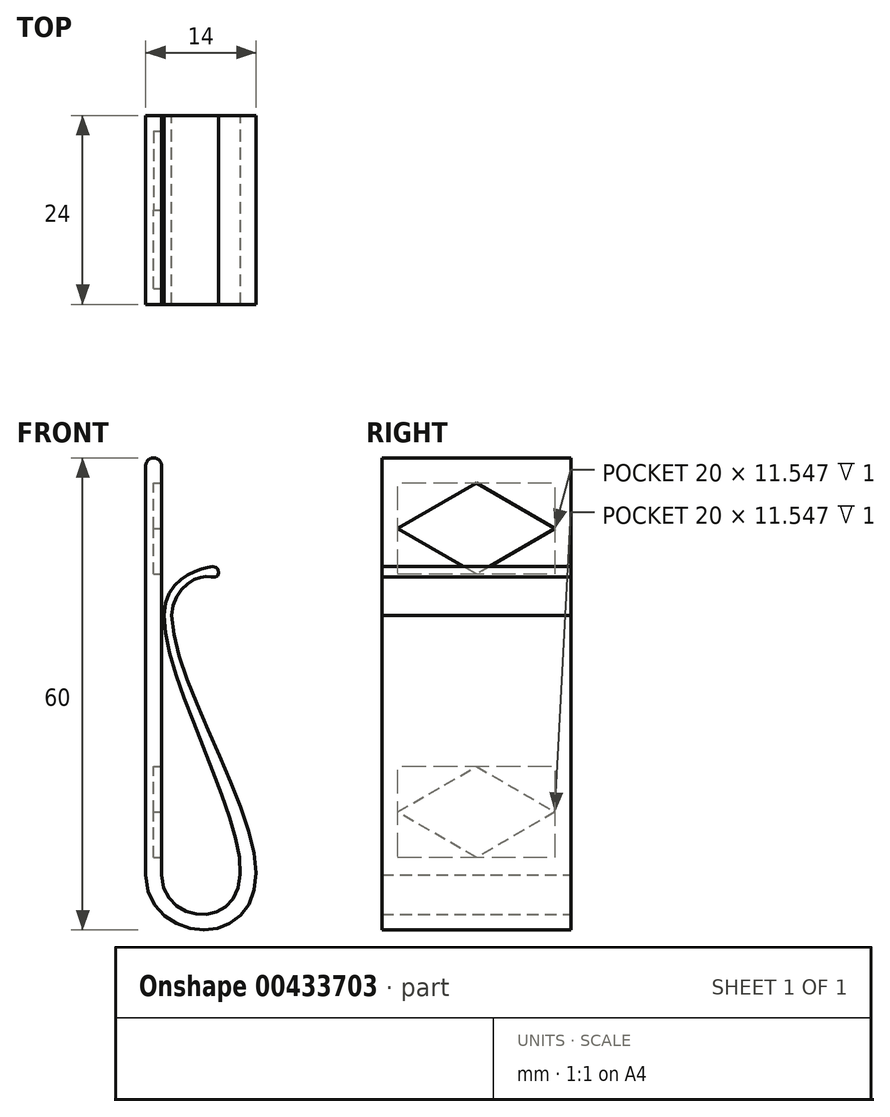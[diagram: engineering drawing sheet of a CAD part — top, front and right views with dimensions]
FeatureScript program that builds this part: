
annotation { "Feature Type Name" : "Feature", "Feature Type Description" : "" }
export const myFeature = defineFeature(function(context is Context, id is Id, definition is map)
    precondition{}
    {
        {
            var Q0;
            Q0=qCreatedBy(makeId("Front.planeOp"),FACE);
            var sketch = newSketch(context, id + "F0", { "sketchPlane" : qUnion([Q0])});
            skLineSegment(sketch, "E0", {"start": v(0, 0) * mm, "end": v(0, 60) * mm});
            skLineSegment(sketch, "E1", {"start": v(0, 60) * mm, "end": v(2, 60) * mm});
            skLineSegment(sketch, "E2", {"start": v(2, 60) * mm, "end": v(2, 6.99) * mm});
            skCircle(sketch, "E3", {"center": v(7, 6.99) * mm, "radius": 5 * mm, "construction": true});
            skPoint(sketch, "E3.second.point", {"position": v(12, 6.99) * mm});
            skPoint(sketch, "E3.third.point", {"position": v(7, 1.99) * mm});
            skLineSegment(sketch, "E4", {"start": v(-15.76, 1.99) * mm, "end": v(42.82, 1.99) * mm, "construction": true});
            skLineSegment(sketch, "E5", {"start": v(-19.4, 40) * mm, "end": v(56.96, 40) * mm, "construction": true});
            skCircle(sketch, "E6", {"center": v(8.3, 40) * mm, "radius": 5 * mm, "construction": true});
            skCircle(sketch, "E7", {"center": v(7, 6.99) * mm, "radius": 7 * mm, "construction": true});
            skPoint(sketch, "E8", {"position": v(14, 6.99) * mm});
            skCircle(sketch, "E9", {"center": v(8.3, 40) * mm, "radius": 6 * mm, "construction": true});
            skFitSpline(sketch, "E10", {"points": [v(2.3, 40) * mm, v(12, 6.99) * mm, v(7, 1.99) * mm, v(2, 6.99) * mm], "startDerivative": vector(0.03, -47.94) * mm, "endDerivative": vector(-1.45, 40.4) * mm});
            skFitSpline(sketch, "E11", {"points": [v(3.3, 40) * mm, v(14, 6.99) * mm, v(7.44, 0) * mm, v(0, 6.99) * mm], "startDerivative": vector(0.62, -51.65) * mm, "endDerivative": vector(0, 51.02) * mm});
            skFitSpline(sketch, "E12", {"points": [v(3.3, 40) * mm, v(7.21, 44.88) * mm, v(9.06, 44.94) * mm, v(9.13, 45.94) * mm, v(7.09, 45.88) * mm, v(2.3, 40) * mm], "startDerivative": vector(0.42, 30.75) * mm, "endDerivative": vector(-1.6, -38.91) * mm});
            skSolve(sketch);
        }
        {
            var Q0;
            Q0 = qSketchRegion(id + "F0", true);
            extrude(context, id + "F1", {"entities" : qUnion([Q0]), "depth" : 24 * mm});
        }
        {
            var Q0;
            Q0=makeQuery(id+"F1.opExtrude","SWEPT_EDGE",EDGE,{"disambiguationData":[OSD([sQuery(id+"F0.wireOp",EDGE,"E1"),sQuery(id+"F0.wireOp",EDGE,"E2")])]});
            var Q1;
            Q1=makeQuery(id+"F1.opExtrude","SWEPT_EDGE",EDGE,{"disambiguationData":[OSD([sQuery(id+"F0.wireOp",EDGE,"E0"),sQuery(id+"F0.wireOp",EDGE,"E1")])]});
            fillet(context, id + "F2", {"entities" : qUnion([Q0, Q1]), "radius" : 1 * mm, "tangentPropagation" : true, "allowEdgeOverflow" : false});
        }
        {
            var Q0;
            Q0=makeQuery(id+"F1.opExtrude","SWEPT_FACE",FACE,{"disambiguationData":[OSD([sQuery(id+"F0.wireOp",EDGE,"E2")])]});
            var sketch = newSketch(context, id + "F3", { "sketchPlane" : qUnion([Q0])});
            skLineSegment(sketch, "E13", {"start": v(-22, 51) * mm, "end": v(-12, 56.77) * mm});
            skLineSegment(sketch, "E14", {"start": v(-12, 56.77) * mm, "end": v(-2, 51) * mm});
            skLineSegment(sketch, "E15", {"start": v(-2, 51) * mm, "end": v(-12, 45.23) * mm});
            skLineSegment(sketch, "E16", {"start": v(-12, 45.23) * mm, "end": v(-22, 51) * mm});
            skLineSegment(sketch, "E17", {"start": v(-12, 58.48) * mm, "end": v(-12, 47.83) * mm, "construction": true});
            skLineSegment(sketch, "E18", {"start": v(-24, 51) * mm, "end": v(0, 51) * mm, "construction": true});
            skPoint(sketch, "E19", {"position": v(-12, 51) * mm});
            skCircle(sketch, "E20", {"center": v(-12, 51) * mm, "radius": 5 * mm, "construction": true});
            skSolve(sketch);
        }
        {
            var Q0;
            Q0=makeQuery(id+"F3.imprint","IMPRINT",FACE,{"disambiguationData":[TD([[makeQuery(id+"F3.imprint","IMPRINT",EDGE,{"derivedFrom":sQuery(id+"F3.wireOp",EDGE,"E13")}),-1.0]])]});
            extrude(context, id + "F4", {"entities" : qUnion([Q0]), "oppositeDirection" : true, "depth" : 1 * mm});
        }
        {
            var Q0;
            Q0=makeQuery(id+"F4.opExtrude","SWEPT_BODY",BODY,{"disambiguationData":[OSD([sQuery(id+"F3.wireOp",EDGE,"E13"),sQuery(id+"F3.wireOp",EDGE,"E14"),sQuery(id+"F3.wireOp",EDGE,"E15"),sQuery(id+"F3.wireOp",EDGE,"E16")])]});
            var Q1;
            Q1=makeQuery(id+"F1.opExtrude","SWEPT_BODY",BODY,{"disambiguationData":[OSD([sQuery(id+"F0.wireOp",EDGE,"E0"),sQuery(id+"F0.wireOp",EDGE,"E1"),sQuery(id+"F0.wireOp",EDGE,"E2"),sQuery(id+"F0.wireOp",EDGE,"E10"),sQuery(id+"F0.wireOp",EDGE,"E11"),sQuery(id+"F0.wireOp",EDGE,"E12")])]});
            booleanBodies(context, id + "F5", {"operationType" : BooleanOperationType.SUBTRACTION, "tools" : qUnion([Q0]), "targets" : qUnion([Q1]), "keepTools" : true});
        }
        {
            var Q0;
            Q0=makeQuery(id+"F4.opExtrude","SWEPT_BODY",BODY,{"disambiguationData":[OSD([sQuery(id+"F3.wireOp",EDGE,"E13"),sQuery(id+"F3.wireOp",EDGE,"E14"),sQuery(id+"F3.wireOp",EDGE,"E15"),sQuery(id+"F3.wireOp",EDGE,"E16")])]});
            transform(context, id + "F6", {"entities" : qUnion([Q0]), "transformType" : TransformType.TRANSLATION_3D, "dx" : 0 * mm, "dy" : 0 * mm, "dz" : -36 * mm, "makeCopy" : false});
        }
        {
            var Q0;
            Q0=makeQuery(id+"F4.opExtrude","SWEPT_BODY",BODY,{"disambiguationData":[OSD([sQuery(id+"F3.wireOp",EDGE,"E13"),sQuery(id+"F3.wireOp",EDGE,"E14"),sQuery(id+"F3.wireOp",EDGE,"E15"),sQuery(id+"F3.wireOp",EDGE,"E16")])]});
            var Q1;
            Q1=makeQuery(id+"F1.opExtrude","SWEPT_BODY",BODY,{"disambiguationData":[OSD([sQuery(id+"F0.wireOp",EDGE,"E0"),sQuery(id+"F0.wireOp",EDGE,"E1"),sQuery(id+"F0.wireOp",EDGE,"E2"),sQuery(id+"F0.wireOp",EDGE,"E10"),sQuery(id+"F0.wireOp",EDGE,"E11"),sQuery(id+"F0.wireOp",EDGE,"E12")])]});
            booleanBodies(context, id + "F7", {"operationType" : BooleanOperationType.SUBTRACTION, "tools" : qUnion([Q0]), "targets" : qUnion([Q1])});
        }
    });
